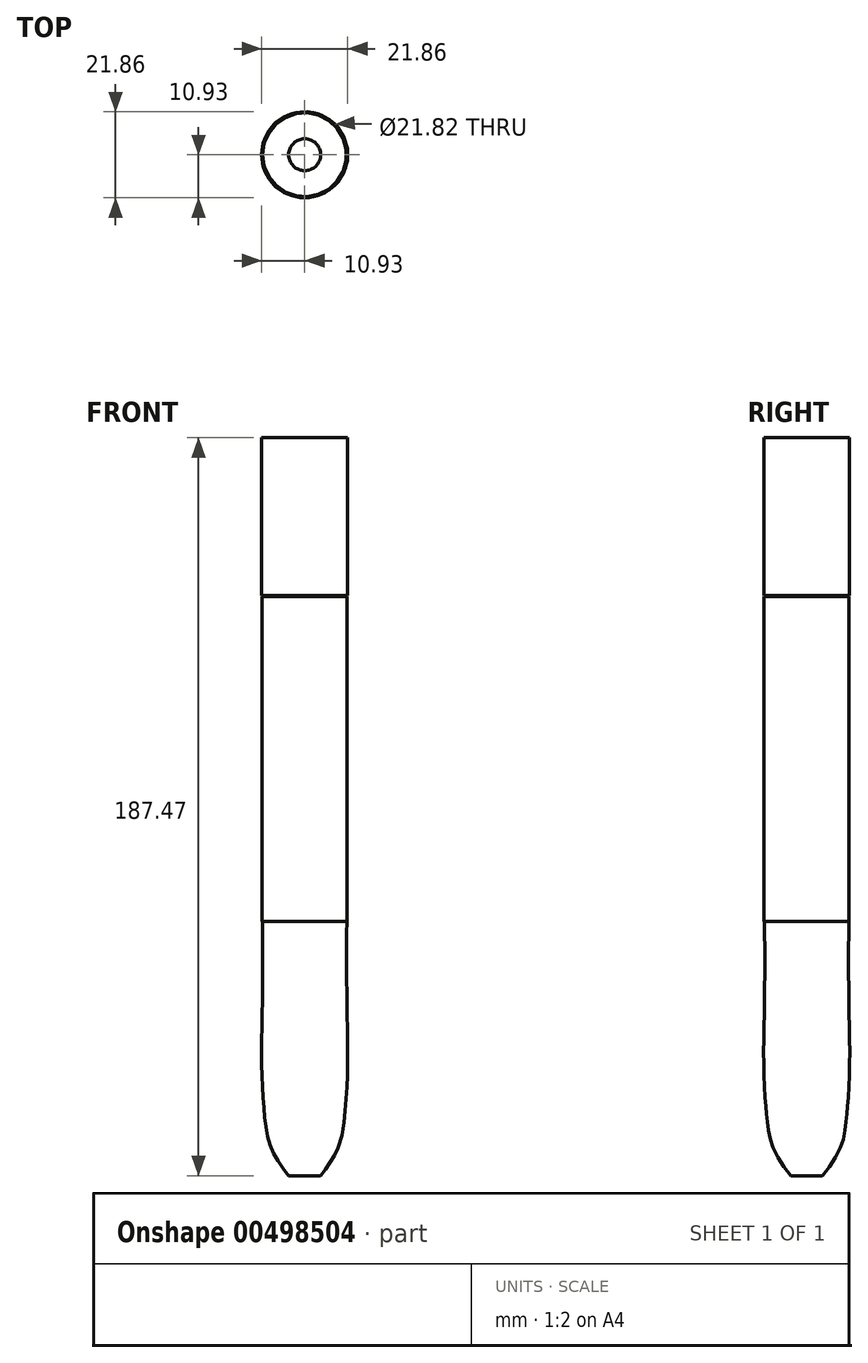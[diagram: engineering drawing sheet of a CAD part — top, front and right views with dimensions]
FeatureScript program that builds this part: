
annotation { "Feature Type Name" : "Feature", "Feature Type Description" : "" }
export const myFeature = defineFeature(function(context is Context, id is Id, definition is map)
    precondition{}
    {
        {
            var Q0;
            Q0=qCreatedBy(makeId("Top.planeOp"),FACE);
            var sketch = newSketch(context, id + "F0", { "sketchPlane" : qUnion([Q0])});
            skCircle(sketch, "E0", {"center": v(0, 0) * mm, "radius": 10.8 * mm});
            skSolve(sketch);
        }
        {
            var Q0;
            Q0=sQuery(id+"F0.wireOp",EDGE,"E0");
            extrude(context, id + "F1", {"bodyType" : ToolBodyType.SURFACE, "surfaceEntities" : qUnion([Q0]), "depth" : 82.55 * mm});
        }
        {
            var Q0;
            Q0=qCreatedBy(makeId("Front.planeOp"),FACE);
            var sketch = newSketch(context, id + "F2", { "sketchPlane" : qUnion([Q0])});
            skLineSegment(sketch, "E1", {"start": v(0, -64.58) * mm, "end": v(4.05, -64.58) * mm});
            skFitSpline(sketch, "E2", {"points": [v(10.7, 0) * mm, v(10.7, -18.44) * mm, v(10.91, -35.9) * mm, v(10.29, -48.16) * mm, v(8.63, -57.3) * mm, v(4.05, -64.58) * mm], "startDerivative": vector(-0.52, -76.86) * mm, "endDerivative": vector(-32.42, -42.53) * mm});
            skSolve(sketch);
        }
        {
            var Q0;
            Q0=qCreatedBy(makeId("Front.planeOp"),FACE);
            var sketch = newSketch(context, id + "F3", { "sketchPlane" : qUnion([Q0])});
            skLineSegment(sketch, "E3", {"start": v(0, 0) * mm, "end": v(0, -72.48) * mm});
            skSolve(sketch);
        }
        {
            var Q0;
            Q0=sQuery(id+"F2.wireOp",EDGE,"E2");
            var Q1;
            Q1=sQuery(id+"F3.wireOp",EDGE,"E3");
            revolve(context, id + "F4", {"bodyType" : ToolBodyType.SURFACE, "surfaceEntities" : qUnion([Q0]), "axis" : qUnion([Q1]), "revolveType" : RevolveType.SYMMETRIC, "angle" : 360 * degree});
        }
        {
            var Q0;
            Q0=qCreatedBy(makeId("Front.planeOp"),FACE);
            var sketch = newSketch(context, id + "F5", { "sketchPlane" : qUnion([Q0])});
            skLineSegment(sketch, "E4", {"start": v(10.91, 82.78) * mm, "end": v(10.91, 122.9) * mm});
            skLineSegment(sketch, "E5", {"start": v(0, 0) * mm, "end": v(0, 134.11) * mm});
            skSolve(sketch);
        }
        {
            var Q0;
            Q0=sQuery(id+"F5.wireOp",EDGE,"E4");
            var Q1;
            Q1=sQuery(id+"F5.wireOp",EDGE,"E5");
            revolve(context, id + "F6", {"bodyType" : ToolBodyType.SURFACE, "surfaceEntities" : qUnion([Q0]), "axis" : qUnion([Q1]), "revolveType" : RevolveType.SYMMETRIC, "angle" : 360 * degree});
        }
    });
